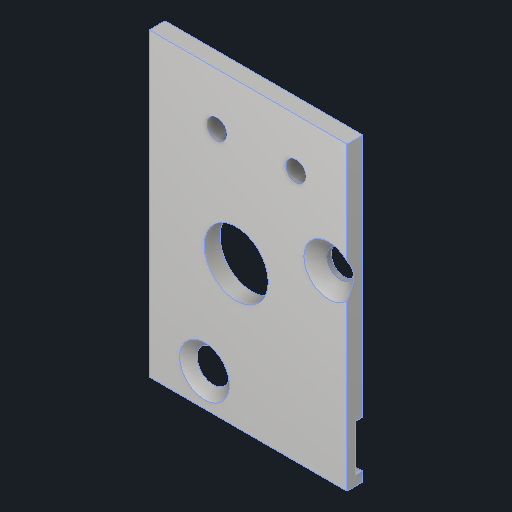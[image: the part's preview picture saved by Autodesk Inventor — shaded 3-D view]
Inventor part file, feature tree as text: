
AUTODESK INVENTOR PART (.ipt)
format: ipt  version: 2023 (Build 270158000, 158)  size: 136,704 bytes
history: native  units: mm
features: reference x6, other x5, extrude x3, sketch x3, hole x1
ambient origin geometry x8: Origin, YZ Plane, XZ Plane, XY Plane, X Axis, Y Axis, Z Axis, Center Point
bodies: Body1 (feature_tree)
feature tree (18):
  other  "Bryła1"
  extrude  "Wyciągnięcie proste1"  Depth=2.0mm TaperAngle=0.0deg
  sketch  "Szkic2"
  extrude  "Wyciągnięcie proste2"  Depth=2.0mm TaperAngle=0.0deg
  hole  "Otwór1"  [1 undecoded]
  extrude  "Wyciągnięcie proste3"  Depth=23.0mm TaperAngle=0.0deg
  sketch  "Szkic1"
  reference  "Odniesienie1"
  reference  "Odniesienie3"
  reference  "Odniesienie4"
  reference  "Odniesienie5"
  sketch  "Szkic3"
  reference  "Odniesienie8"
  reference  "Odniesienie9"
  parser-record x1  (decoder bookkeeping rows leaked as tree rows — omitted from the tree; the rows remain in map.json)
  other  "PrzekladniaPrawa.iam"
  other  "MocowaniePrawejPrzekladni:1"
  other  "Oś:1"
note: 1 required parameter value undecoded (feature->parameter linkage not recoverable at this tier; creation-order binding heuristic only, values carry confidence <= 0.55)
note: 1 file-system path scrubbed to <path> (originals preserved in map.json)
